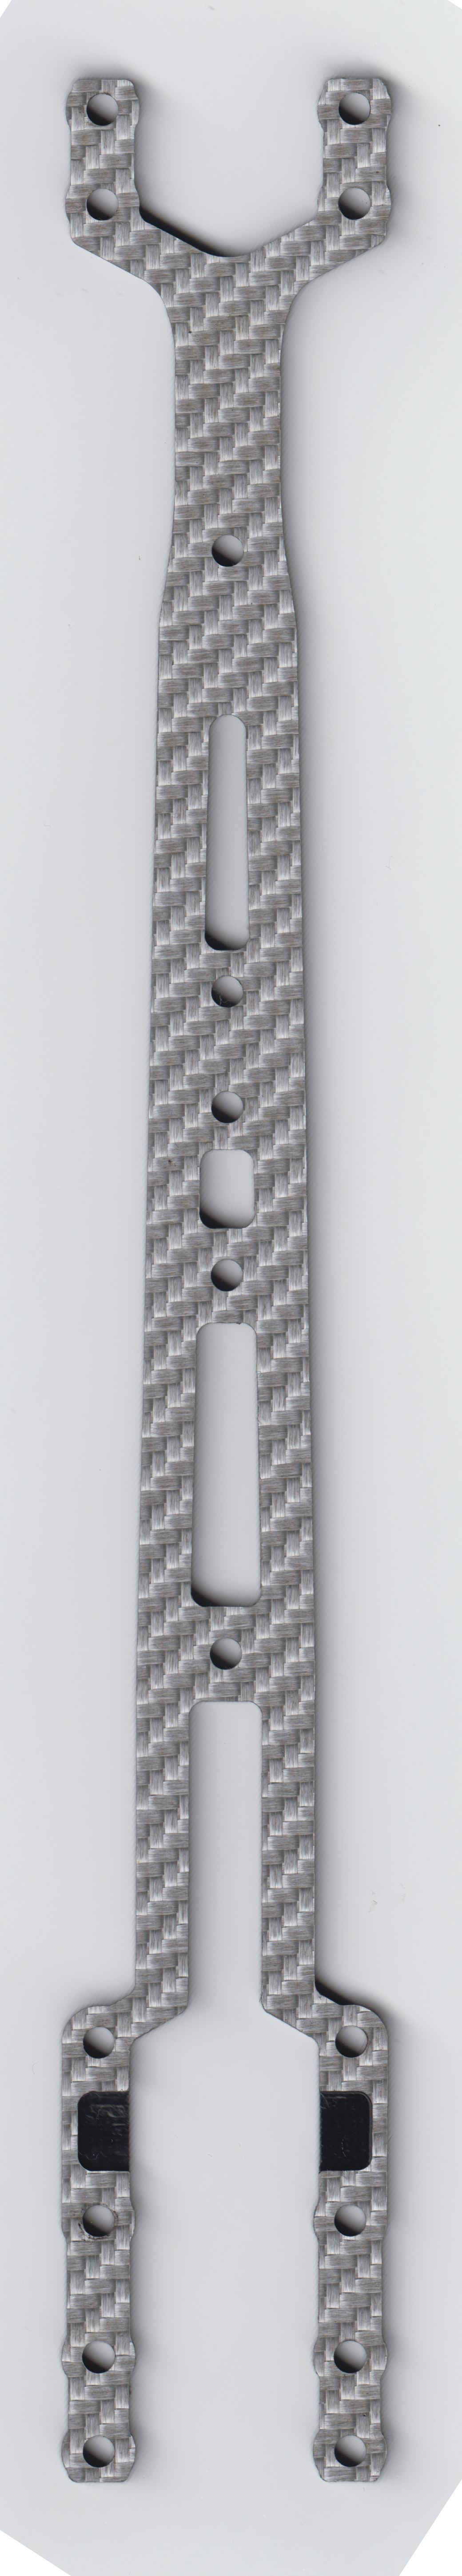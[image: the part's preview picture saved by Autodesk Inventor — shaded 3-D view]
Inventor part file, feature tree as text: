
AUTODESK INVENTOR PART (.ipt)
format: ipt  version: 2021 (Build 250183000, 183)  size: 11,065,344 bytes
history: native  units: mm
features: other x7, extrude x2, sketch x1
ambient origin geometry x8: Origin, YZ Plane, XZ Plane, XY Plane, X Axis, Y Axis, Z Axis, Center Point
bodies: Body1 (feature_tree)
feature tree (10):
  other  "original"
  other  "dim_aligned"
  other  "shortened"
  other  "top_plate"
  extrude  "plate"  Depth=5.0mm
  extrude  "bearing_recess"  Depth=5.0mm
  other  "bearing_recess_outline"
  other  "Image1"
  other  "top_plate_fillets"
  sketch  "Sketch8"  dims[d52=3.1mm d57=3.1mm d61=3.1mm d70=3.1mm d78=3.1mm d82=3.1mm d86=3.1mm d88=3.1mm d92=3.1mm d96=3.1mm d100=3.1mm d103=3.1mm d109=3.1mm d111=3.1mm d115=3.1mm d119=3.1mm d122=3.1mm d128=7.559983mm d129=5.125066mm d137=7.6406mm d138=4.868365mm d146=16.467534mm d152=44.011135mm d169=150.0deg d170=30.0deg d177=16.886287mm d178=18.218522mm d193=150.0deg d197=229.041984mm d198=41.867869mm d199=74.448359mm d200=32.58049mm d201=12.792042mm d202=18.01385mm d203=16.977039mm d204=17.992193mm d205=5.20015mm d208=12.0mm d209=12.0mm d210=0.0mm d211=0.0mm d212=12.0mm d213=12.0mm d214=9.0mm d215=9.0mm d216=12.0mm d217=12.0mm d218=22.0mm d219=22.0mm d220=39.0mm d221=39.0mm d222=12.0mm d223=12.0mm d224=12.0mm d225=12.0mm d226=0.0mm d227=0.0mm d228=9.0mm d229=9.0mm d230=12.0mm d231=12.0mm d232=76.0mm d233=42.0mm d234=112.0mm d235=128.1mm d236=139.1mm d237=12.0mm d238=12.0mm d239=0.0mm d240=0.0mm d241=12.0mm d242=12.0mm d243=9.0mm d244=9.0mm d245=12.0mm d246=12.0mm d247=22.0mm d248=22.0mm d249=39.0mm d250=39.0mm d251=12.0mm d252=12.0mm d253=12.0mm d254=12.0mm d255=0.0mm d256=0.0mm d257=9.0mm d258=9.0mm d259=12.0mm d260=12.0mm d263=161.246205mm d264=38.653059mm d265=25.16502mm d267=2.8mm d268=2.8mm d269=0.0mm d273=3.1mm d278=17.6mm d280=11.0mm d288=6.980624mm d289=32.58049mm d292=7.0mm d293=150.0deg d294=41.9mm d295=76.0mm d297=150.0deg d298=3.6mm d300=17.0mm d301=2.7mm d302=10.0mm d304=28.0mm d306=4.0mm d312=3.1mm d314=7.0mm d329=24.0mm d340=6.0mm d341=8.0mm d342=5.2mm d343=5.2mm d344=8.0mm d345=29.706748mm d346=29.607019mm d347=17.0mm d348=8.5mm d349=29.3mm d350=3.1mm d359=3.0mm d360=3.0mm d361=0.0mm d364=3.0mm d366=3.0mm d368=0.0mm d369=3.0mm d373=3.0mm d377=3.0mm d378=3.0mm d379=3.0mm d380=3.0mm d381=3.0mm d382=2.0mm d396=4.0mm d397=4.0mm d398=0.0mm d399=3.0mm d415=3.0mm d418=3.0mm d450=31.0mm d452=24.0mm d453=3.0mm d454=3.0mm d455=2.0mm d456=2.0mm d457=2.0mm d458=2.0mm d459=3.0mm d460=3.0mm d461=3.0mm d462=3.0mm d463=3.0mm d464=3.0mm d465=45.1mm d466=3.1mm d470=3.0mm d471=3.0mm d472=3.0mm d473=3.0mm d479=166.846205mm d480=46.0mm d483=4.0mm d486=3.0mm d487=0.0mm d488=1.0mm d489=0.0mm d492=36.0mm d503=9.0mm d508=26.0mm d511=3.0mm d512=3.0mm d516=3.1mm d517=3.1mm d518=4.0mm d519=0.0mm d520=10.0mm d522=3.1mm d524=70.6mm d525=60.0mm d526=19.0mm d527=4.0mm d532=3.1mm d533=16.0mm d534=52.0mm d535=3.0mm d536=3.1mm d537=3.1mm d538=32.0mm d540=45.646205mm d541=6.823102mm d542=2.0mm d543=4.0mm d544=3.0mm d545=3.0mm d546=4.0mm d547=4.0mm d548=3.0mm d549=3.0mm d550=4.0mm d551=4.0mm d552=3.0mm d553=3.0mm d554=3.0mm d555=6.0mm d556=3.1mm d557=10.0mm d558=3.1mm d559=3.1mm d560=30.0mm d561=3.1mm d562=30.0mm d566=5.0mm d567=5.0mm d578=81.046205mm d385=0.5mm d386=0.872665mm d387=0.5mm d388=0.872665mm d400=0.5mm d401=0.872665mm d402=0.5mm d403=0.872665mm d491=0.5mm d493=0.5mm d494=0.872665mm]
